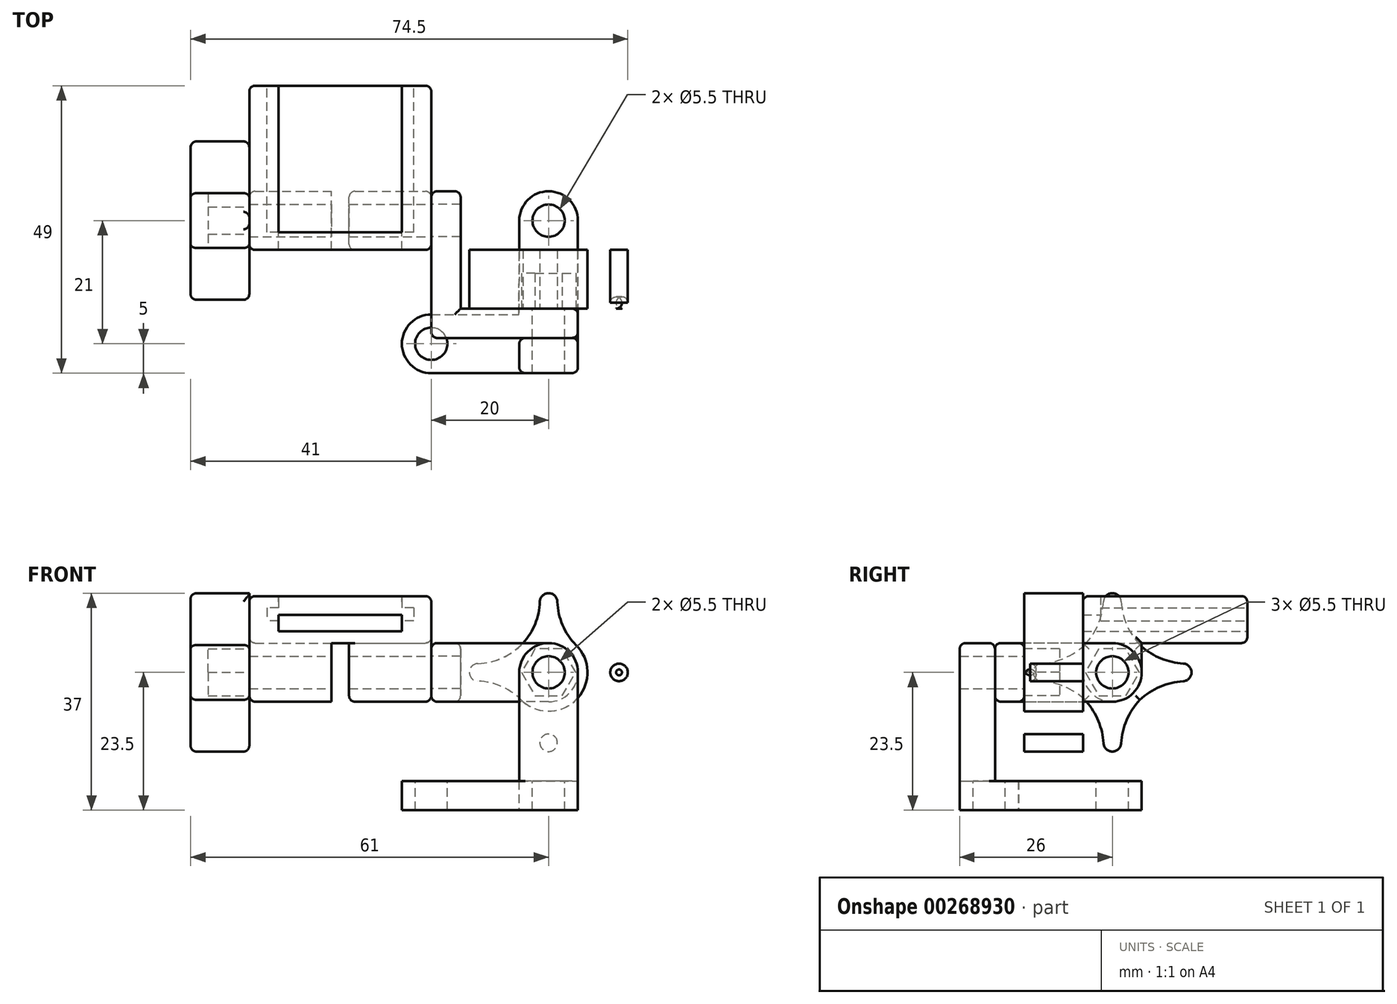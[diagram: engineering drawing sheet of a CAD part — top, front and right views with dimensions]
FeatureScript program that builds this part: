
annotation { "Feature Type Name" : "Feature", "Feature Type Description" : "" }
export const myFeature = defineFeature(function(context is Context, id is Id, definition is map)
    precondition{}
    {
        {
            var Q0;
            Q0=qCreatedBy(makeId("Top.planeOp"),FACE);
            var sketch = newSketch(context, id + "F0", { "sketchPlane" : qUnion([Q0])});
            skLineSegment(sketch, "E0.bottom", {"start": v(-15.5, 14) * mm, "end": v(15.5, 14) * mm});
            skLineSegment(sketch, "E0.top", {"start": v(-15.5, -14) * mm, "end": v(15.5, -14) * mm});
            skLineSegment(sketch, "E0.left", {"start": v(-15.5, 14) * mm, "end": v(-15.5, -14) * mm});
            skLineSegment(sketch, "E0.right", {"start": v(15.5, 14) * mm, "end": v(15.5, -14) * mm});
            skPoint(sketch, "E1", {"position": v(0, 14) * mm});
            skPoint(sketch, "E2", {"position": v(-15.5, 0) * mm});
            skSolve(sketch);
        }
        {
            var Q0;
            Q0=makeQuery(id+"F0.imprint","IMPRINT",FACE,{"disambiguationData":[TD([[makeQuery(id+"F0.imprint","IMPRINT",EDGE,{"derivedFrom":sQuery(id+"F0.wireOp",EDGE,"E0.bottom")}),-1.0]])]});
            extrude(context, id + "F1", {"entities" : qUnion([Q0]), "depth" : (4 + 4) * mm});
        }
        {
            var Q0;
            Q0=makeQuery(id+"F1.opExtrude","SWEPT_FACE",FACE,{"disambiguationData":[OSD([sQuery(id+"F0.wireOp",EDGE,"E0.bottom")])]});
            var sketch = newSketch(context, id + "F2", { "sketchPlane" : qUnion([Q0])});
            skLineSegment(sketch, "E3.bottom", {"start": v(-12.5, 6) * mm, "end": v(12.5, 6) * mm});
            skLineSegment(sketch, "E3.top", {"start": v(-12.5, 4.8) * mm, "end": v(12.5, 4.8) * mm});
            skLineSegment(sketch, "E3.left", {"start": v(-12.5, 6) * mm, "end": v(-12.5, 4.8) * mm});
            skLineSegment(sketch, "E3.right", {"start": v(12.5, 6) * mm, "end": v(12.5, 4.8) * mm});
            skLineSegment(sketch, "E4.bottom", {"start": v(-10.5, 8) * mm, "end": v(10.5, 8) * mm});
            skLineSegment(sketch, "E4.top", {"start": v(-10.5, 2) * mm, "end": v(10.5, 2) * mm});
            skLineSegment(sketch, "E4.left", {"start": v(-10.5, 8) * mm, "end": v(-10.5, 2) * mm});
            skLineSegment(sketch, "E4.right", {"start": v(10.5, 8) * mm, "end": v(10.5, 2) * mm});
            skSolve(sketch);
        }
        {
            var Q0;
            {var subQ5=sQuery(id+"F2.wireOp",EDGE,"E4.bottom");Q0=makeQuery(id+"F2.imprint","IMPRINT",FACE,{"disambiguationData":[TD([[makeQuery(id+"F2.imprint","IMPRINT",EDGE,{"derivedFrom":subQ5}),1.0]])]});}
            var Q1;
            {var subQ0=sQuery(id+"F2.wireOp",EDGE,"E4.left");var subQ1=sQuery(id+"F2.wireOp",EDGE,"E3.bottom");var subQ2=makeQuery(id+"F2.imprint","INTERSECT",VERTEX,{"derivedFrom":[subQ1,subQ0]});Q1=makeQuery(id+"F2.imprint","IMPRINT",FACE,{"disambiguationData":[TD([[makeQuery(id+"F2.imprint","IMPRINT",EDGE,{"disambiguationData":[TD([[subQ2,-1.0]])],"derivedFrom":subQ1}),-1.0]])]});}
            var Q2;
            {var subQ0=sQuery(id+"F2.wireOp",EDGE,"E3.left");Q2=makeQuery(id+"F2.imprint","IMPRINT",FACE,{"disambiguationData":[TD([[makeQuery(id+"F2.imprint","IMPRINT",EDGE,{"derivedFrom":subQ0}),1.0]])]});}
            var Q3;
            {var subQ5=sQuery(id+"F2.wireOp",EDGE,"E4.top");Q3=makeQuery(id+"F2.imprint","IMPRINT",FACE,{"disambiguationData":[TD([[makeQuery(id+"F2.imprint","IMPRINT",EDGE,{"derivedFrom":subQ5}),1.0]])]});}
            var Q4;
            {var subQ0=sQuery(id+"F2.wireOp",EDGE,"E3.right");Q4=makeQuery(id+"F2.imprint","IMPRINT",FACE,{"disambiguationData":[TD([[makeQuery(id+"F2.imprint","IMPRINT",EDGE,{"derivedFrom":subQ0}),-1.0]])]});}
            extrude(context, id + "F3", {"entities" : qUnion([Q0, Q1, Q2, Q3, Q4]), "operationType" : NewBodyOperationType.REMOVE, "oppositeDirection" : true, "depth" : 25 * mm});
        }
        {
            var Q0;
            Q0=makeQuery(id+"F3.boolean.opBoolean","COPY",FACE,{"derivedFrom":makeQuery(id+"F3.opExtrude","CAP_FACE",FACE,{"disambiguationData":[OSD([sQuery(id+"F2.wireOp",EDGE,"E3.bottom"),sQuery(id+"F2.wireOp",EDGE,"E3.top"),sQuery(id+"F2.wireOp",EDGE,"E3.left"),sQuery(id+"F2.wireOp",EDGE,"E3.right"),sQuery(id+"F2.wireOp",EDGE,"E4.bottom"),sQuery(id+"F2.wireOp",EDGE,"E4.top"),sQuery(id+"F2.wireOp",EDGE,"E4.left"),sQuery(id+"F2.wireOp",EDGE,"E4.right")])],"isStart":false})});
            var sketch = newSketch(context, id + "F4", { "sketchPlane" : qUnion([Q0])});
            skLineSegment(sketch, "E5.bottom", {"start": v(-10.5, 4.8) * mm, "end": v(10.5, 4.8) * mm});
            skLineSegment(sketch, "E5.top", {"start": v(-10.5, 2) * mm, "end": v(10.5, 2) * mm});
            skLineSegment(sketch, "E5.left", {"start": v(-10.5, 4.8) * mm, "end": v(-10.5, 2) * mm});
            skLineSegment(sketch, "E5.right", {"start": v(10.5, 4.8) * mm, "end": v(10.5, 2) * mm});
            skSolve(sketch);
        }
        {
            var Q0;
            Q0=makeQuery(id+"F4.imprint","IMPRINT",FACE,{"disambiguationData":[TD([[makeQuery(id+"F4.imprint","IMPRINT",EDGE,{"derivedFrom":sQuery(id+"F4.wireOp",EDGE,"E5.bottom")}),-1.0]])]});
            extrude(context, id + "F5", {"entities" : qUnion([Q0]), "operationType" : NewBodyOperationType.REMOVE, "endBound" : BoundingType.UP_TO_NEXT, "oppositeDirection" : true, "depth" : 25 * mm});
        }
        {
            var Q0;
            Q0=makeQuery(id+"F1.opExtrude","SWEPT_FACE",FACE,{"disambiguationData":[OSD([sQuery(id+"F0.wireOp",EDGE,"E0.right")])]});
            var sketch = newSketch(context, id + "F6", { "sketchPlane" : qUnion([Q0])});
            skLineSegment(sketch, "E6.bottom", {"start": v(-14, 0) * mm, "end": v(-4, 0) * mm});
            skLineSegment(sketch, "E6.top", {"start": v(-14, -10) * mm, "end": v(-4, -10) * mm});
            skLineSegment(sketch, "E6.left", {"start": v(-14, 0) * mm, "end": v(-14, -10) * mm});
            skLineSegment(sketch, "E6.right", {"start": v(-4, 0) * mm, "end": v(-4, -10) * mm});
            skCircle(sketch, "E7", {"center": v(-9, -5) * mm, "radius": 2.75 * mm});
            skPoint(sketch, "E8", {"position": v(-4, -5) * mm});
            skPoint(sketch, "E9", {"position": v(-9, -10) * mm});
            skCircle(sketch, "E10", {"center": v(-9, -5) * mm, "radius": 5 * mm});
            skSolve(sketch);
        }
        {
            var Q0;
            Q0=makeQuery(id+"F6.imprint","IMPRINT",FACE,{"disambiguationData":[TD([[makeQuery(id+"F6.imprint","IMPRINT",EDGE,{"derivedFrom":sQuery(id+"F6.wireOp",EDGE,"E7")}),-1.0]])]});
            var Q1;
            {var subQ0=sQuery(id+"F6.wireOp",EDGE,"E6.left");var subQ3=sQuery(id+"F6.wireOp",EDGE,"E10");var subQ5=makeQuery(id+"F6.imprint","INTERSECT",VERTEX,{"derivedFrom":[subQ0,subQ3]});Q1=makeQuery(id+"F6.imprint","IMPRINT",FACE,{"disambiguationData":[TD([[makeQuery(id+"F6.imprint","IMPRINT",EDGE,{"disambiguationData":[TD([[subQ5,1.0]])],"derivedFrom":subQ3}),-1.0]])]});}
            var Q2;
            {var subQ0=sQuery(id+"F6.wireOp",EDGE,"E6.right");var subQ3=sQuery(id+"F6.wireOp",EDGE,"E10");var subQ5=makeQuery(id+"F6.imprint","INTERSECT",VERTEX,{"derivedFrom":[subQ0,subQ3]});Q2=makeQuery(id+"F6.imprint","IMPRINT",FACE,{"disambiguationData":[TD([[makeQuery(id+"F6.imprint","IMPRINT",EDGE,{"disambiguationData":[TD([[subQ5,-1.0]])],"derivedFrom":subQ3}),-1.0]])]});}
            var Q3;
            Q3=makeQuery(id+"F1.opExtrude","SWEPT_FACE",FACE,{"disambiguationData":[OSD([sQuery(id+"F0.wireOp",EDGE,"E0.left")])]});
            extrude(context, id + "F7", {"entities" : qUnion([Q0, Q1, Q2]), "operationType" : NewBodyOperationType.ADD, "endBound" : BoundingType.UP_TO_SURFACE, "oppositeDirection" : true, "endBoundEntityFace" : qUnion([Q3]), "depth" : 25 * mm});
        }
        {
            var Q0;
            Q0=makeQuery(id+"F7.opExtrude","SWEPT_FACE",FACE,{"disambiguationData":[OSD([sQuery(id+"F6.wireOp",EDGE,"E6.right")])]});
            var sketch = newSketch(context, id + "F8", { "sketchPlane" : qUnion([Q0])});
            skLineSegment(sketch, "E11.bottom", {"start": v(-1.5, 0) * mm, "end": v(1.5, 0) * mm});
            skLineSegment(sketch, "E11.top", {"start": v(-1.5, -11.71) * mm, "end": v(1.5, -11.71) * mm});
            skLineSegment(sketch, "E11.left", {"start": v(-1.5, 0) * mm, "end": v(-1.5, -11.71) * mm});
            skLineSegment(sketch, "E11.right", {"start": v(1.5, 0) * mm, "end": v(1.5, -11.71) * mm});
            skPoint(sketch, "E12", {"position": v(0, 0) * mm});
            skSolve(sketch);
        }
        {
            var Q0;
            {var subQ0=sQuery(id+"F2.wireOp",EDGE,"E3.top");Q0=makeQuery(id+"F3.boolean.opBoolean","COPY",FACE,{"derivedFrom":makeQuery(id+"F3.opExtrude","SWEPT_FACE",FACE,{"disambiguationData":[OSD([subQ0]),TDD([makeQuery(id+"F2.imprint","IMPRINT",EDGE,{"disambiguationData":[TD([[makeQuery(id+"F2.imprint","INTERSECT",VERTEX,{"derivedFrom":[subQ0,sQuery(id+"F2.wireOp",EDGE,"E3.right")]}),1.0]])],"derivedFrom":subQ0})])]})});}
            var Q1;
            {var subQ0=sQuery(id+"F2.wireOp",EDGE,"E3.top");Q1=makeQuery(id+"F3.boolean.opBoolean","COPY",FACE,{"derivedFrom":makeQuery(id+"F3.opExtrude","SWEPT_FACE",FACE,{"disambiguationData":[OSD([subQ0]),TDD([makeQuery(id+"F2.imprint","IMPRINT",EDGE,{"disambiguationData":[TD([[makeQuery(id+"F2.imprint","INTERSECT",VERTEX,{"derivedFrom":[subQ0,sQuery(id+"F2.wireOp",EDGE,"E3.left")]}),-1.0]])],"derivedFrom":subQ0})])]})});}
            extrude(context, id + "F9", {"entities" : qUnion([Q0, Q1]), "operationType" : NewBodyOperationType.REMOVE, "oppositeDirection" : true, "depth" : 1 * mm});
        }
        {
            var Q0;
            {var subQ0=sQuery(id+"F8.wireOp",EDGE,"E11.bottom");Q0=makeQuery(id+"F8.imprint","IMPRINT",FACE,{"disambiguationData":[TD([[makeQuery(id+"F8.imprint","IMPRINT",EDGE,{"derivedFrom":subQ0}),1.0]])]});}
            var Q1;
            {var subQ0=sQuery(id+"F8.wireOp",EDGE,"E11.top");Q1=makeQuery(id+"F8.imprint","IMPRINT",FACE,{"disambiguationData":[TD([[makeQuery(id+"F8.imprint","IMPRINT",EDGE,{"derivedFrom":subQ0}),1.0]])]});}
            extrude(context, id + "F10", {"entities" : qUnion([Q0, Q1]), "operationType" : NewBodyOperationType.REMOVE, "endBound" : BoundingType.THROUGH_ALL, "oppositeDirection" : true, "depth" : 25 * mm});
        }
        {
            var Q0;
            Q0=makeQuery(id+"F1.opExtrude","CAP_EDGE",EDGE,{"disambiguationData":[OSD([sQuery(id+"F0.wireOp",EDGE,"E0.left")])],"isStart":false});
            var Q1;
            Q1=makeQuery(id+"F1.opExtrude","CAP_EDGE",EDGE,{"disambiguationData":[OSD([sQuery(id+"F0.wireOp",EDGE,"E0.left")])],"isStart":true});
            var Q2;
            Q2=makeQuery(id+"F1.opExtrude","CAP_EDGE",EDGE,{"disambiguationData":[OSD([sQuery(id+"F0.wireOp",EDGE,"E0.right")])],"isStart":true});
            var Q3;
            Q3=makeQuery(id+"F1.opExtrude","CAP_EDGE",EDGE,{"disambiguationData":[OSD([sQuery(id+"F0.wireOp",EDGE,"E0.right")])],"isStart":false});
            var Q4;
            Q4=makeQuery(id+"F3.boolean.opBoolean","COPY",EDGE,{"derivedFrom":makeQuery(id+"F3.opExtrude","SWEPT_EDGE",EDGE,{"disambiguationData":[OSD([sQuery(id+"F0.wireOp",EDGE,"E0.bottom"),sQuery(id+"F2.wireOp",EDGE,"E4.bottom"),sQuery(id+"F2.wireOp",EDGE,"E4.right")])]})});
            var Q5;
            Q5=makeQuery(id+"F3.boolean.opBoolean","COPY",EDGE,{"derivedFrom":makeQuery(id+"F3.opExtrude","SWEPT_EDGE",EDGE,{"disambiguationData":[OSD([sQuery(id+"F0.wireOp",EDGE,"E0.bottom"),sQuery(id+"F2.wireOp",EDGE,"E4.bottom"),sQuery(id+"F2.wireOp",EDGE,"E4.left")])]})});
            var Q6;
            Q6=makeQuery(id+"F3.boolean.opBoolean","COPY",EDGE,{"derivedFrom":makeQuery(id+"F3.opExtrude","CAP_EDGE",EDGE,{"disambiguationData":[OSD([sQuery(id+"F2.wireOp",EDGE,"E4.bottom")])],"isStart":false})});
            var Q7;
            Q7=makeQuery(id+"F5.boolean.opBoolean","COPY",EDGE,{"derivedFrom":makeQuery(id+"F5.opExtrude","CAP_EDGE",EDGE,{"disambiguationData":[OSD([sQuery(id+"F4.wireOp",EDGE,"E5.bottom")])],"isStart":true})});
            var Q8;
            Q8=makeQuery(id+"F1.opExtrude","CAP_EDGE",EDGE,{"disambiguationData":[OSD([sQuery(id+"F0.wireOp",EDGE,"E0.bottom")])],"isStart":true});
            var Q9;
            Q9=makeQuery(id+"F1.opExtrude","SWEPT_EDGE",EDGE,{"disambiguationData":[OSD([sQuery(id+"F0.wireOp",EDGE,"E0.bottom"),sQuery(id+"F0.wireOp",EDGE,"E0.left")])]});
            var Q10;
            Q10=makeQuery(id+"F1.opExtrude","SWEPT_EDGE",EDGE,{"disambiguationData":[OSD([sQuery(id+"F0.wireOp",EDGE,"E0.bottom"),sQuery(id+"F0.wireOp",EDGE,"E0.right")])]});
            var Q11;
            {var subQ0=sQuery(id+"F0.wireOp",EDGE,"E0.bottom");var subQ2=makeQuery(id+"F1.opExtrude","CAP_EDGE",EDGE,{"disambiguationData":[OSD([subQ0])],"isStart":false});var subQ3=sQuery(id+"F0.wireOp",EDGE,"E0.right");Q11=makeQuery(id+"F3.boolean.opBoolean","SPLIT",EDGE,{"disambiguationData":[TD([makeQuery(id+"F1.opExtrude","SWEPT_FACE",FACE,{"disambiguationData":[OSD([subQ3])]})])],"derivedFrom":subQ2});}
            var Q12;
            {var subQ0=sQuery(id+"F0.wireOp",EDGE,"E0.bottom");var subQ1=sQuery(id+"F0.wireOp",EDGE,"E0.left");var subQ3=makeQuery(id+"F1.opExtrude","CAP_EDGE",EDGE,{"disambiguationData":[OSD([subQ0])],"isStart":false});Q12=makeQuery(id+"F3.boolean.opBoolean","SPLIT",EDGE,{"disambiguationData":[TD([makeQuery(id+"F1.opExtrude","SWEPT_FACE",FACE,{"disambiguationData":[OSD([subQ1])]})])],"derivedFrom":subQ3});}
            var Q13;
            Q13=makeQuery(id+"F3.boolean.opBoolean","COPY",EDGE,{"derivedFrom":makeQuery(id+"F3.opExtrude","CAP_EDGE",EDGE,{"disambiguationData":[OSD([sQuery(id+"F2.wireOp",EDGE,"E4.top")])],"isStart":true})});
            var Q14;
            {var subQ0=sQuery(id+"F2.wireOp",EDGE,"E4.left");Q14=makeQuery(id+"F3.boolean.opBoolean","COPY",EDGE,{"derivedFrom":makeQuery(id+"F3.opExtrude","CAP_EDGE",EDGE,{"disambiguationData":[OSD([subQ0]),TDD([makeQuery(id+"F2.imprint","IMPRINT",EDGE,{"disambiguationData":[TD([[makeQuery(id+"F2.imprint","INTERSECT",VERTEX,{"derivedFrom":[sQuery(id+"F2.wireOp",EDGE,"E4.top"),subQ0]}),1.0]])],"derivedFrom":subQ0})])],"isStart":true})});}
            var Q15;
            {var subQ0=sQuery(id+"F2.wireOp",EDGE,"E4.right");Q15=makeQuery(id+"F3.boolean.opBoolean","COPY",EDGE,{"derivedFrom":makeQuery(id+"F3.opExtrude","CAP_EDGE",EDGE,{"disambiguationData":[OSD([subQ0]),TDD([makeQuery(id+"F2.imprint","IMPRINT",EDGE,{"disambiguationData":[TD([[makeQuery(id+"F2.imprint","INTERSECT",VERTEX,{"derivedFrom":[sQuery(id+"F2.wireOp",EDGE,"E4.top"),subQ0]}),1.0]])],"derivedFrom":subQ0})])],"isStart":true})});}
            var Q16;
            Q16=makeQuery(id+"F3.boolean.opBoolean","COPY",EDGE,{"derivedFrom":makeQuery(id+"F3.opExtrude","CAP_EDGE",EDGE,{"disambiguationData":[OSD([sQuery(id+"F2.wireOp",EDGE,"E3.left")])],"isStart":true})});
            var Q17;
            {var subQ0=sQuery(id+"F2.wireOp",EDGE,"E3.top");Q17=makeQuery(id+"F3.boolean.opBoolean","COPY",EDGE,{"derivedFrom":makeQuery(id+"F3.opExtrude","CAP_EDGE",EDGE,{"disambiguationData":[OSD([subQ0]),TDD([makeQuery(id+"F2.imprint","IMPRINT",EDGE,{"disambiguationData":[TD([[makeQuery(id+"F2.imprint","INTERSECT",VERTEX,{"derivedFrom":[subQ0,sQuery(id+"F2.wireOp",EDGE,"E3.left")]}),-1.0]])],"derivedFrom":subQ0})])],"isStart":true})});}
            var Q18;
            {var subQ0=sQuery(id+"F2.wireOp",EDGE,"E3.bottom");Q18=makeQuery(id+"F3.boolean.opBoolean","COPY",EDGE,{"derivedFrom":makeQuery(id+"F3.opExtrude","CAP_EDGE",EDGE,{"disambiguationData":[OSD([subQ0]),TDD([makeQuery(id+"F2.imprint","IMPRINT",EDGE,{"disambiguationData":[TD([[makeQuery(id+"F2.imprint","INTERSECT",VERTEX,{"derivedFrom":[subQ0,sQuery(id+"F2.wireOp",EDGE,"E3.left")]}),-1.0]])],"derivedFrom":subQ0})])],"isStart":true})});}
            var Q19;
            Q19=makeQuery(id+"F3.boolean.opBoolean","COPY",EDGE,{"derivedFrom":makeQuery(id+"F3.opExtrude","CAP_EDGE",EDGE,{"disambiguationData":[OSD([sQuery(id+"F2.wireOp",EDGE,"E3.right")])],"isStart":true})});
            var Q20;
            {var subQ0=sQuery(id+"F2.wireOp",EDGE,"E3.top");Q20=makeQuery(id+"F3.boolean.opBoolean","COPY",EDGE,{"derivedFrom":makeQuery(id+"F3.opExtrude","CAP_EDGE",EDGE,{"disambiguationData":[OSD([subQ0]),TDD([makeQuery(id+"F2.imprint","IMPRINT",EDGE,{"disambiguationData":[TD([[makeQuery(id+"F2.imprint","INTERSECT",VERTEX,{"derivedFrom":[subQ0,sQuery(id+"F2.wireOp",EDGE,"E3.right")]}),1.0]])],"derivedFrom":subQ0})])],"isStart":true})});}
            var Q21;
            {var subQ0=sQuery(id+"F2.wireOp",EDGE,"E3.bottom");Q21=makeQuery(id+"F3.boolean.opBoolean","COPY",EDGE,{"derivedFrom":makeQuery(id+"F3.opExtrude","CAP_EDGE",EDGE,{"disambiguationData":[OSD([subQ0]),TDD([makeQuery(id+"F2.imprint","IMPRINT",EDGE,{"disambiguationData":[TD([[makeQuery(id+"F2.imprint","INTERSECT",VERTEX,{"derivedFrom":[subQ0,sQuery(id+"F2.wireOp",EDGE,"E3.right")]}),1.0]])],"derivedFrom":subQ0})])],"isStart":true})});}
            var Q22;
            {var subQ0=sQuery(id+"F2.wireOp",EDGE,"E4.right");Q22=makeQuery(id+"F3.boolean.opBoolean","COPY",EDGE,{"derivedFrom":makeQuery(id+"F3.opExtrude","CAP_EDGE",EDGE,{"disambiguationData":[OSD([subQ0]),TDD([makeQuery(id+"F2.imprint","IMPRINT",EDGE,{"disambiguationData":[TD([[makeQuery(id+"F2.imprint","INTERSECT",VERTEX,{"derivedFrom":[sQuery(id+"F2.wireOp",EDGE,"E3.bottom"),subQ0]}),1.0]])],"derivedFrom":subQ0})])],"isStart":true})});}
            var Q23;
            {var subQ0=sQuery(id+"F2.wireOp",EDGE,"E4.left");Q23=makeQuery(id+"F3.boolean.opBoolean","COPY",EDGE,{"derivedFrom":makeQuery(id+"F3.opExtrude","CAP_EDGE",EDGE,{"disambiguationData":[OSD([subQ0]),TDD([makeQuery(id+"F2.imprint","IMPRINT",EDGE,{"disambiguationData":[TD([[makeQuery(id+"F2.imprint","INTERSECT",VERTEX,{"derivedFrom":[sQuery(id+"F2.wireOp",EDGE,"E3.bottom"),subQ0]}),1.0]])],"derivedFrom":subQ0})])],"isStart":true})});}
            var Q24;
            Q24=makeQuery(id+"F5.boolean.opBoolean","COPY",EDGE,{"derivedFrom":makeQuery(id+"F5.opExtrude","TWEAK_EDGE",EDGE,{"derivedFrom":[makeQuery(id+"F1.opExtrude","SWEPT_FACE",FACE,{"disambiguationData":[OSD([sQuery(id+"F0.wireOp",EDGE,"E0.top")])]}),makeQuery(id+"F4.imprint","IMPRINT",EDGE,{"derivedFrom":sQuery(id+"F4.wireOp",EDGE,"E5.top")})]})});
            var Q25;
            Q25=makeQuery(id+"F5.boolean.opBoolean","COPY",EDGE,{"derivedFrom":makeQuery(id+"F5.opExtrude","TWEAK_EDGE",EDGE,{"derivedFrom":[makeQuery(id+"F1.opExtrude","SWEPT_FACE",FACE,{"disambiguationData":[OSD([sQuery(id+"F0.wireOp",EDGE,"E0.top")])]}),makeQuery(id+"F4.imprint","IMPRINT",EDGE,{"derivedFrom":sQuery(id+"F4.wireOp",EDGE,"E5.bottom")})]})});
            var Q26;
            Q26=makeQuery(id+"F5.boolean.opBoolean","COPY",EDGE,{"derivedFrom":makeQuery(id+"F5.opExtrude","TWEAK_EDGE",EDGE,{"derivedFrom":[makeQuery(id+"F1.opExtrude","SWEPT_FACE",FACE,{"disambiguationData":[OSD([sQuery(id+"F0.wireOp",EDGE,"E0.top")])]}),makeQuery(id+"F4.imprint","IMPRINT",EDGE,{"derivedFrom":sQuery(id+"F4.wireOp",EDGE,"E5.left")})]})});
            var Q27;
            Q27=makeQuery(id+"F5.boolean.opBoolean","COPY",EDGE,{"derivedFrom":makeQuery(id+"F5.opExtrude","TWEAK_EDGE",EDGE,{"derivedFrom":[makeQuery(id+"F1.opExtrude","SWEPT_FACE",FACE,{"disambiguationData":[OSD([sQuery(id+"F0.wireOp",EDGE,"E0.top")])]}),makeQuery(id+"F4.imprint","IMPRINT",EDGE,{"derivedFrom":sQuery(id+"F4.wireOp",EDGE,"E5.right")})]})});
            var Q28;
            Q28=makeQuery(id+"F1.opExtrude","CAP_EDGE",EDGE,{"disambiguationData":[OSD([sQuery(id+"F0.wireOp",EDGE,"E0.top")])],"isStart":false});
            var Q29;
            Q29=makeQuery(id+"F1.opExtrude","SWEPT_EDGE",EDGE,{"disambiguationData":[OSD([sQuery(id+"F0.wireOp",EDGE,"E0.top"),sQuery(id+"F0.wireOp",EDGE,"E0.right")])]});
            var Q30;
            Q30=makeQuery(id+"F1.opExtrude","CAP_EDGE",EDGE,{"disambiguationData":[OSD([sQuery(id+"F0.wireOp",EDGE,"E0.top")])],"isStart":true});
            var Q31;
            Q31=makeQuery(id+"F1.opExtrude","SWEPT_EDGE",EDGE,{"disambiguationData":[OSD([sQuery(id+"F0.wireOp",EDGE,"E0.top"),sQuery(id+"F0.wireOp",EDGE,"E0.left")])]});
            var Q32;
            Q32=makeQuery(id+"F10.boolean.opBoolean","COPY",EDGE,{"derivedFrom":makeQuery(id+"F10.opExtrude","CAP_EDGE",EDGE,{"disambiguationData":[OSD([sQuery(id+"F8.wireOp",EDGE,"E11.left")])],"isStart":true})});
            var Q33;
            Q33=makeQuery(id+"F10.boolean.opBoolean","COPY",EDGE,{"derivedFrom":makeQuery(id+"F10.opExtrude","CAP_EDGE",EDGE,{"disambiguationData":[OSD([sQuery(id+"F8.wireOp",EDGE,"E11.right")])],"isStart":true})});
            var Q34;
            {var subQ0=sQuery(id+"F2.wireOp",EDGE,"E3.top");Q34=makeQuery(id+"F9.boolean.opBoolean","COPY",EDGE,{"derivedFrom":makeQuery(id+"F9.opExtrude","CAP_EDGE",EDGE,{"disambiguationData":[OSD([subQ0]),TDD([makeQuery(id+"F3.boolean.opBoolean","COPY",EDGE,{"derivedFrom":makeQuery(id+"F3.opExtrude","CAP_EDGE",EDGE,{"disambiguationData":[OSD([subQ0]),TDD([makeQuery(id+"F2.imprint","IMPRINT",EDGE,{"disambiguationData":[TD([[makeQuery(id+"F2.imprint","INTERSECT",VERTEX,{"derivedFrom":[subQ0,sQuery(id+"F2.wireOp",EDGE,"E3.right")]}),1.0]])],"derivedFrom":subQ0})])],"isStart":true})})])],"isStart":false})});}
            var Q35;
            {var subQ0=sQuery(id+"F2.wireOp",EDGE,"E3.top");Q35=makeQuery(id+"F9.boolean.opBoolean","COPY",EDGE,{"derivedFrom":makeQuery(id+"F9.opExtrude","CAP_EDGE",EDGE,{"disambiguationData":[OSD([subQ0]),TDD([makeQuery(id+"F3.boolean.opBoolean","COPY",EDGE,{"derivedFrom":makeQuery(id+"F3.opExtrude","CAP_EDGE",EDGE,{"disambiguationData":[OSD([subQ0]),TDD([makeQuery(id+"F2.imprint","IMPRINT",EDGE,{"disambiguationData":[TD([[makeQuery(id+"F2.imprint","INTERSECT",VERTEX,{"derivedFrom":[subQ0,sQuery(id+"F2.wireOp",EDGE,"E3.left")]}),-1.0]])],"derivedFrom":subQ0})])],"isStart":true})})])],"isStart":false})});}
            fillet(context, id + "F11", {"entities" : qUnion([Q0, Q1, Q2, Q3, Q4, Q5, Q6, Q7, Q8, Q9, Q10, Q11, Q12, Q13, Q14, Q15, Q16, Q17, Q18, Q19, Q20, Q21, Q22, Q23, Q24, Q25, Q26, Q27, Q28, Q29, Q30, Q31, Q32, Q33, Q34, Q35]), "radius" : 1 * mm, "tangentPropagation" : true, "allowEdgeOverflow" : false});
        }
        {
            var Q0;
            {var subQ0=sQuery(id+"F0.wireOp",EDGE,"E0.left");Q0=makeQuery(id+"F7.boolean.opBoolean","MERGE",FACE,{"derivedFrom":[makeQuery(id+"F1.opExtrude","SWEPT_FACE",FACE,{"disambiguationData":[OSD([subQ0])]}),makeQuery(id+"F7.opExtrude","CAP_FACE",FACE,{"disambiguationData":[OSD([subQ0])],"isStart":false})]});}
            var sketch = newSketch(context, id + "F12", { "sketchPlane" : qUnion([Q0])});
            skCircle(sketch, "E13.cCircle", {"center": v(9, -5) * mm, "radius": 4 * mm, "construction": true});
            skLineSegment(sketch, "E13.0", {"start": v(6.7, -1) * mm, "end": v(11.3, -1) * mm});
            skLineSegment(sketch, "E13.1", {"start": v(11.3, -1) * mm, "end": v(13.62, -5) * mm});
            skLineSegment(sketch, "E13.2", {"start": v(13.62, -5) * mm, "end": v(11.3, -9) * mm});
            skLineSegment(sketch, "E13.3", {"start": v(11.3, -9) * mm, "end": v(6.7, -9) * mm});
            skLineSegment(sketch, "E13.4", {"start": v(6.7, -9) * mm, "end": v(4.38, -5) * mm});
            skLineSegment(sketch, "E13.5", {"start": v(4.38, -5) * mm, "end": v(6.7, -1) * mm});
            skPoint(sketch, "E13.0.midPoint", {"position": v(9, -1) * mm});
            skCircle(sketch, "E14", {"center": v(9, -5) * mm, "radius": 6.62 * mm});
            skCircle(sketch, "E15", {"center": v(9, 7) * mm, "radius": 1.5 * mm});
            skLineSegment(sketch, "E16", {"start": v(9, -5) * mm, "end": v(4.32, -0.32) * mm});
            skLineSegment(sketch, "E17", {"start": v(9, -5) * mm, "end": v(13.68, -0.32) * mm});
            skArc(sketch, "E18", {"start": v(4.32, -0.32) * mm, "mid": v(6.55, 3.11) * mm, "end": v(7.5, 7.1) * mm});
            skArc(sketch, "E19", {"start": v(10.5, 7.1) * mm, "mid": v(11.45, 3.11) * mm, "end": v(13.68, -0.32) * mm});
            skArc(sketch, "E20.1.0", {"start": v(-3.1, -3.5) * mm, "mid": v(0.89, -2.55) * mm, "end": v(4.32, -0.32) * mm});
            skArc(sketch, "E20.1.1", {"start": v(4.32, -9.68) * mm, "mid": v(0.89, -7.45) * mm, "end": v(-3.1, -6.5) * mm});
            skCircle(sketch, "E20.1.2", {"center": v(-3, -5) * mm, "radius": 1.5 * mm});
            skArc(sketch, "E20.2.0", {"start": v(7.5, -17.1) * mm, "mid": v(6.55, -13.11) * mm, "end": v(4.32, -9.68) * mm});
            skArc(sketch, "E20.2.1", {"start": v(13.68, -9.68) * mm, "mid": v(11.45, -13.11) * mm, "end": v(10.5, -17.1) * mm});
            skCircle(sketch, "E20.2.2", {"center": v(9, -17) * mm, "radius": 1.5 * mm});
            skArc(sketch, "E20.3.0", {"start": v(21.1, -6.5) * mm, "mid": v(17.11, -7.45) * mm, "end": v(13.68, -9.68) * mm});
            skArc(sketch, "E20.3.1", {"start": v(13.68, -0.32) * mm, "mid": v(17.11, -2.55) * mm, "end": v(21.1, -3.5) * mm});
            skCircle(sketch, "E20.3.2", {"center": v(21, -5) * mm, "radius": 1.5 * mm});
            skSolve(sketch);
        }
        {
            var Q0;
            {var subQ1=sQuery(id+"F0.wireOp",EDGE,"E0.left");var subQ2=makeQuery(id+"F1.opExtrude","SWEPT_FACE",FACE,{"disambiguationData":[OSD([subQ1])]});var subQ3=makeQuery(id+"F7.boolean.opBoolean","MERGE",FACE,{"derivedFrom":[subQ2,makeQuery(id+"F7.opExtrude","CAP_FACE",FACE,{"disambiguationData":[OSD([subQ1])],"isStart":false})]});var subQ4=makeQuery(id+"F11.opFillet","BLEND_EDGE",EDGE,{"blendedFrom":[makeQuery(id+"F1.opExtrude","CAP_EDGE",EDGE,{"disambiguationData":[OSD([subQ1])],"isStart":false}),subQ3],"blendedInto":[subQ3]});var subQ18=sQuery(id+"F12.wireOp",EDGE,"E15");var subQ19=makeQuery(id+"F12.imprint","INTERSECT",VERTEX,{"disambiguationData":[OD(0.0)],"derivedFrom":[subQ4,subQ18]});Q0=makeQuery(id+"F12.imprint","IMPRINT",FACE,{"disambiguationData":[TD([[makeQuery(id+"F12.imprint","IMPRINT",EDGE,{"disambiguationData":[TD([[subQ19,-1.0]])],"derivedFrom":subQ18}),-1.0]])]});}
            var Q1;
            {var subQ0=sQuery(id+"F12.wireOp",EDGE,"E15");var subQ1=sQuery(id+"F0.wireOp",EDGE,"E0.left");var subQ2=makeQuery(id+"F11.opFillet","BLEND_EDGE",EDGE,{"blendedFrom":[makeQuery(id+"F1.opExtrude","CAP_EDGE",EDGE,{"disambiguationData":[OSD([subQ1])],"isStart":false}),makeQuery(id+"F7.boolean.opBoolean","MERGE",FACE,{"derivedFrom":[makeQuery(id+"F1.opExtrude","SWEPT_FACE",FACE,{"disambiguationData":[OSD([subQ1])]}),makeQuery(id+"F7.opExtrude","CAP_FACE",FACE,{"disambiguationData":[OSD([subQ1])],"isStart":false})]})],"blendedInto":[makeQuery(id+"F7.boolean.opBoolean","MERGE",FACE,{"derivedFrom":[makeQuery(id+"F1.opExtrude","SWEPT_FACE",FACE,{"disambiguationData":[OSD([subQ1])]}),makeQuery(id+"F7.opExtrude","CAP_FACE",FACE,{"disambiguationData":[OSD([subQ1])],"isStart":false})]})]});var subQ3=makeQuery(id+"F12.imprint","INTERSECT",VERTEX,{"disambiguationData":[OD(0.0)],"derivedFrom":[subQ2,subQ0]});Q1=makeQuery(id+"F12.imprint","IMPRINT",FACE,{"disambiguationData":[TD([[makeQuery(id+"F12.imprint","IMPRINT",EDGE,{"disambiguationData":[TD([[subQ3,-1.0]])],"derivedFrom":subQ0}),1.0]])]});}
            var Q2;
            {var subQ0=sQuery(id+"F12.wireOp",EDGE,"E15");var subQ1=makeQuery(id+"F12.imprint","INTERSECT",VERTEX,{"derivedFrom":[subQ0,sQuery(id+"F12.wireOp",EDGE,"E18")]});Q2=makeQuery(id+"F12.imprint","IMPRINT",FACE,{"disambiguationData":[TD([[makeQuery(id+"F12.imprint","IMPRINT",EDGE,{"disambiguationData":[TD([[subQ1,1.0]])],"derivedFrom":subQ0}),1.0]])]});}
            var Q3;
            {var subQ0=sQuery(id+"F12.wireOp",EDGE,"E20.1.2");var subQ1=makeQuery(id+"F12.imprint","INTERSECT",VERTEX,{"derivedFrom":[sQuery(id+"F12.wireOp",EDGE,"E20.1.0"),subQ0]});Q3=makeQuery(id+"F12.imprint","IMPRINT",FACE,{"disambiguationData":[TD([[makeQuery(id+"F12.imprint","IMPRINT",EDGE,{"disambiguationData":[TD([[subQ1,-1.0]])],"derivedFrom":subQ0}),1.0]])]});}
            var Q4;
            {var subQ0=sQuery(id+"F12.wireOp",EDGE,"E20.1.0");Q4=makeQuery(id+"F12.imprint","IMPRINT",FACE,{"disambiguationData":[TD([[makeQuery(id+"F12.imprint","IMPRINT",EDGE,{"derivedFrom":subQ0}),-1.0]])]});}
            var Q5;
            {var subQ0=sQuery(id+"F12.wireOp",EDGE,"E20.2.0");Q5=makeQuery(id+"F12.imprint","IMPRINT",FACE,{"disambiguationData":[TD([[makeQuery(id+"F12.imprint","IMPRINT",EDGE,{"derivedFrom":subQ0}),-1.0]])]});}
            var Q6;
            {var subQ0=sQuery(id+"F12.wireOp",EDGE,"E20.2.2");var subQ1=makeQuery(id+"F12.imprint","INTERSECT",VERTEX,{"derivedFrom":[sQuery(id+"F12.wireOp",EDGE,"E20.2.0"),subQ0]});Q6=makeQuery(id+"F12.imprint","IMPRINT",FACE,{"disambiguationData":[TD([[makeQuery(id+"F12.imprint","IMPRINT",EDGE,{"disambiguationData":[TD([[subQ1,-1.0]])],"derivedFrom":subQ0}),1.0]])]});}
            var Q7;
            {var subQ2=sQuery(id+"F12.wireOp",EDGE,"E20.3.0");Q7=makeQuery(id+"F12.imprint","IMPRINT",FACE,{"disambiguationData":[TD([[makeQuery(id+"F12.imprint","IMPRINT",EDGE,{"derivedFrom":subQ2}),-1.0]])]});}
            var Q8;
            {var subQ0=sQuery(id+"F12.wireOp",EDGE,"E20.3.2");var subQ1=makeQuery(id+"F12.imprint","INTERSECT",VERTEX,{"derivedFrom":[sQuery(id+"F12.wireOp",EDGE,"E20.3.0"),subQ0]});Q8=makeQuery(id+"F12.imprint","IMPRINT",FACE,{"disambiguationData":[TD([[makeQuery(id+"F12.imprint","IMPRINT",EDGE,{"disambiguationData":[TD([[subQ1,-1.0]])],"derivedFrom":subQ0}),1.0]])]});}
            var Q9;
            {var subQ0=sQuery(id+"F12.wireOp",EDGE,"E14");var subQ1=makeQuery(id+"F12.imprint","INTERSECT",VERTEX,{"derivedFrom":[subQ0,sQuery(id+"F12.wireOp",EDGE,"E20.1.1"),sQuery(id+"F12.wireOp",EDGE,"E20.2.0")]});Q9=makeQuery(id+"F12.imprint","IMPRINT",FACE,{"disambiguationData":[TD([[makeQuery(id+"F12.imprint","IMPRINT",EDGE,{"disambiguationData":[TD([[subQ1,-1.0]])],"derivedFrom":subQ0}),1.0]])]});}
            var Q10;
            {var subQ19=sQuery(id+"F12.wireOp",EDGE,"E13.0");Q10=makeQuery(id+"F12.imprint","IMPRINT",FACE,{"disambiguationData":[TD([[makeQuery(id+"F12.imprint","IMPRINT",EDGE,{"derivedFrom":subQ19}),1.0]])]});}
            var Q11;
            {var subQ0=sQuery(id+"F12.wireOp",EDGE,"E18");var subQ1=sQuery(id+"F12.wireOp",EDGE,"E14");var subQ2=makeQuery(id+"F12.imprint","INTERSECT",VERTEX,{"derivedFrom":[subQ1,sQuery(id+"F12.wireOp",EDGE,"E16"),subQ0,sQuery(id+"F12.wireOp",EDGE,"E20.1.0")]});Q11=makeQuery(id+"F12.imprint","IMPRINT",FACE,{"disambiguationData":[TD([[makeQuery(id+"F12.imprint","IMPRINT",EDGE,{"disambiguationData":[TD([[subQ2,1.0]])],"derivedFrom":subQ1}),-1.0]])]});}
            var Q12;
            {var subQ0=sQuery(id+"F12.wireOp",EDGE,"E16");var subQ1=sQuery(id+"F12.wireOp",EDGE,"E13.5");var subQ2=makeQuery(id+"F12.imprint","INTERSECT",VERTEX,{"derivedFrom":[subQ1,subQ0]});Q12=makeQuery(id+"F12.imprint","IMPRINT",FACE,{"disambiguationData":[TD([[makeQuery(id+"F12.imprint","IMPRINT",EDGE,{"disambiguationData":[TD([[subQ2,1.0]])],"derivedFrom":subQ1}),1.0]])]});}
            var Q13;
            {var subQ0=sQuery(id+"F12.wireOp",EDGE,"E16");var subQ1=sQuery(id+"F12.wireOp",EDGE,"E14");var subQ2=makeQuery(id+"F12.imprint","INTERSECT",VERTEX,{"derivedFrom":[subQ1,subQ0,sQuery(id+"F12.wireOp",EDGE,"E18"),sQuery(id+"F12.wireOp",EDGE,"E20.1.0")]});Q13=makeQuery(id+"F12.imprint","IMPRINT",FACE,{"disambiguationData":[TD([[makeQuery(id+"F12.imprint","IMPRINT",EDGE,{"disambiguationData":[TD([[subQ2,1.0]])],"derivedFrom":subQ1}),1.0]])]});}
            var Q14;
            {var subQ0=sQuery(id+"F12.wireOp",EDGE,"E17");var subQ1=sQuery(id+"F12.wireOp",EDGE,"E13.1");var subQ2=makeQuery(id+"F12.imprint","INTERSECT",VERTEX,{"derivedFrom":[subQ1,subQ0]});Q14=makeQuery(id+"F12.imprint","IMPRINT",FACE,{"disambiguationData":[TD([[makeQuery(id+"F12.imprint","IMPRINT",EDGE,{"disambiguationData":[TD([[subQ2,-1.0]])],"derivedFrom":subQ1}),1.0]])]});}
            var Q15;
            {var subQ0=sQuery(id+"F12.wireOp",EDGE,"E17");var subQ1=sQuery(id+"F12.wireOp",EDGE,"E14");var subQ2=makeQuery(id+"F12.imprint","INTERSECT",VERTEX,{"derivedFrom":[subQ1,subQ0,sQuery(id+"F12.wireOp",EDGE,"E19"),sQuery(id+"F12.wireOp",EDGE,"E20.3.1")]});Q15=makeQuery(id+"F12.imprint","IMPRINT",FACE,{"disambiguationData":[TD([[makeQuery(id+"F12.imprint","IMPRINT",EDGE,{"disambiguationData":[TD([[subQ2,-1.0]])],"derivedFrom":subQ1}),1.0]])]});}
            var Q16;
            {var subQ0=sQuery(id+"F12.wireOp",EDGE,"E19");var subQ1=sQuery(id+"F12.wireOp",EDGE,"E14");var subQ2=makeQuery(id+"F12.imprint","INTERSECT",VERTEX,{"derivedFrom":[subQ1,sQuery(id+"F12.wireOp",EDGE,"E17"),subQ0,sQuery(id+"F12.wireOp",EDGE,"E20.3.1")]});Q16=makeQuery(id+"F12.imprint","IMPRINT",FACE,{"disambiguationData":[TD([[makeQuery(id+"F12.imprint","IMPRINT",EDGE,{"disambiguationData":[TD([[subQ2,-1.0]])],"derivedFrom":subQ1}),-1.0]])]});}
            var Q17;
            {var subQ0=sQuery(id+"F12.wireOp",EDGE,"E18");var subQ1=sQuery(id+"F12.wireOp",EDGE,"E15");var subQ2=makeQuery(id+"F12.imprint","INTERSECT",VERTEX,{"derivedFrom":[subQ1,subQ0]});Q17=makeQuery(id+"F12.imprint","IMPRINT",FACE,{"disambiguationData":[TD([[makeQuery(id+"F12.imprint","IMPRINT",EDGE,{"disambiguationData":[TD([[subQ2,-1.0]])],"derivedFrom":subQ1}),-1.0]])]});}
            var Q18;
            {var subQ0=sQuery(id+"F12.wireOp",EDGE,"E19");var subQ1=sQuery(id+"F12.wireOp",EDGE,"E15");var subQ2=makeQuery(id+"F12.imprint","INTERSECT",VERTEX,{"derivedFrom":[subQ1,subQ0]});Q18=makeQuery(id+"F12.imprint","IMPRINT",FACE,{"disambiguationData":[TD([[makeQuery(id+"F12.imprint","IMPRINT",EDGE,{"disambiguationData":[TD([[subQ2,1.0]])],"derivedFrom":subQ1}),-1.0]])]});}
            var Q19;
            {var subQ1=sQuery(id+"F0.wireOp",EDGE,"E0.left");var subQ2=makeQuery(id+"F1.opExtrude","SWEPT_FACE",FACE,{"disambiguationData":[OSD([subQ1])]});var subQ3=makeQuery(id+"F7.boolean.opBoolean","MERGE",FACE,{"derivedFrom":[subQ2,makeQuery(id+"F7.opExtrude","CAP_FACE",FACE,{"disambiguationData":[OSD([subQ1])],"isStart":false})]});var subQ4=makeQuery(id+"F11.opFillet","BLEND_EDGE",EDGE,{"blendedFrom":[makeQuery(id+"F1.opExtrude","CAP_EDGE",EDGE,{"disambiguationData":[OSD([subQ1])],"isStart":false}),subQ3],"blendedInto":[subQ3]});var subQ18=sQuery(id+"F12.wireOp",EDGE,"E15");var subQ20=makeQuery(id+"F12.imprint","INTERSECT",VERTEX,{"disambiguationData":[OD(0.0)],"derivedFrom":[subQ4,subQ18]});Q19=makeQuery(id+"F12.imprint","IMPRINT",FACE,{"disambiguationData":[TD([[makeQuery(id+"F12.imprint","IMPRINT",EDGE,{"disambiguationData":[TD([[subQ20,1.0]])],"derivedFrom":subQ18}),-1.0]])]});}
            var Q20;
            {var subQ0=sQuery(id+"F12.wireOp",EDGE,"E15");var subQ1=sQuery(id+"F0.wireOp",EDGE,"E0.left");var subQ2=makeQuery(id+"F11.opFillet","BLEND_EDGE",EDGE,{"blendedFrom":[makeQuery(id+"F1.opExtrude","CAP_EDGE",EDGE,{"disambiguationData":[OSD([subQ1])],"isStart":false}),makeQuery(id+"F7.boolean.opBoolean","MERGE",FACE,{"derivedFrom":[makeQuery(id+"F1.opExtrude","SWEPT_FACE",FACE,{"disambiguationData":[OSD([subQ1])]}),makeQuery(id+"F7.opExtrude","CAP_FACE",FACE,{"disambiguationData":[OSD([subQ1])],"isStart":false})]})],"blendedInto":[makeQuery(id+"F7.boolean.opBoolean","MERGE",FACE,{"derivedFrom":[makeQuery(id+"F1.opExtrude","SWEPT_FACE",FACE,{"disambiguationData":[OSD([subQ1])]}),makeQuery(id+"F7.opExtrude","CAP_FACE",FACE,{"disambiguationData":[OSD([subQ1])],"isStart":false})]})]});var subQ3=makeQuery(id+"F12.imprint","INTERSECT",VERTEX,{"disambiguationData":[OD(0.0)],"derivedFrom":[subQ2,subQ0]});Q20=makeQuery(id+"F12.imprint","IMPRINT",FACE,{"disambiguationData":[TD([[makeQuery(id+"F12.imprint","IMPRINT",EDGE,{"disambiguationData":[TD([[subQ3,1.0]])],"derivedFrom":subQ0}),1.0]])]});}
            extrude(context, id + "F13", {"entities" : qUnion([Q0, Q1, Q2, Q3, Q4, Q5, Q6, Q7, Q8, Q9, Q10, Q11, Q12, Q13, Q14, Q15, Q16, Q17, Q18, Q19, Q20]), "depth" : 10 * mm});
        }
        {
            var Q0;
            Q0=makeQuery(id+"F13.opExtrude","CAP_FACE",FACE,{"disambiguationData":[OSD([sQuery(id+"F0.wireOp",EDGE,"E0.left"),sQuery(id+"F12.wireOp",EDGE,"E13.0"),sQuery(id+"F12.wireOp",EDGE,"E13.1"),sQuery(id+"F12.wireOp",EDGE,"E13.2"),sQuery(id+"F12.wireOp",EDGE,"E13.3"),sQuery(id+"F12.wireOp",EDGE,"E13.4"),sQuery(id+"F12.wireOp",EDGE,"E13.5"),sQuery(id+"F12.wireOp",EDGE,"E15"),sQuery(id+"F12.wireOp",EDGE,"E18"),sQuery(id+"F12.wireOp",EDGE,"E19"),sQuery(id+"F12.wireOp",EDGE,"E20.1.0"),sQuery(id+"F12.wireOp",EDGE,"E20.1.1"),sQuery(id+"F12.wireOp",EDGE,"E20.1.2"),sQuery(id+"F12.wireOp",EDGE,"E20.2.0"),sQuery(id+"F12.wireOp",EDGE,"E20.2.1"),sQuery(id+"F12.wireOp",EDGE,"E20.2.2"),sQuery(id+"F12.wireOp",EDGE,"E20.3.0"),sQuery(id+"F12.wireOp",EDGE,"E20.3.1"),sQuery(id+"F12.wireOp",EDGE,"E20.3.2")])],"isStart":false});
            var sketch = newSketch(context, id + "F14", { "sketchPlane" : qUnion([Q0])});
            skCircle(sketch, "E21", {"center": v(9, -5) * mm, "radius": 2.75 * mm});
            skSolve(sketch);
        }
        {
            var Q0;
            Q0=makeQuery(id+"F14.imprint","IMPRINT",FACE,{"disambiguationData":[TD([[makeQuery(id+"F14.imprint","IMPRINT",EDGE,{"derivedFrom":makeQuery(id+"F13.opExtrude","CAP_EDGE",EDGE,{"disambiguationData":[OSD([sQuery(id+"F12.wireOp",EDGE,"E13.0")])],"isStart":false})}),-1.0]])]});
            var Q1;
            Q1=makeQuery(id+"F14.imprint","IMPRINT",FACE,{"disambiguationData":[TD([[makeQuery(id+"F14.imprint","IMPRINT",EDGE,{"derivedFrom":sQuery(id+"F14.wireOp",EDGE,"E21")}),1.0]])]});
            extrude(context, id + "F15", {"entities" : qUnion([Q0, Q1]), "operationType" : NewBodyOperationType.ADD, "oppositeDirection" : true, "depth" : 3 * mm});
        }
        {
            var Q0;
            Q0=makeQuery(id+"F7.boolean.opBoolean","MERGE",FACE,{"derivedFrom":[makeQuery(id+"F1.opExtrude","SWEPT_FACE",FACE,{"disambiguationData":[OSD([sQuery(id+"F0.wireOp",EDGE,"E0.right")])]}),makeQuery(id+"F7.opExtrude","CAP_FACE",FACE,{"disambiguationData":[OSD([sQuery(id+"F6.wireOp",EDGE,"E6.bottom"),sQuery(id+"F6.wireOp",EDGE,"E6.left"),sQuery(id+"F6.wireOp",EDGE,"E6.right"),sQuery(id+"F6.wireOp",EDGE,"E7"),sQuery(id+"F6.wireOp",EDGE,"E10")])],"isStart":true})]});
            var sketch = newSketch(context, id + "F16", { "sketchPlane" : qUnion([Q0])});
            skCircle(sketch, "E22", {"center": v(-9, -5) * mm, "radius": 5 * mm});
            skCircle(sketch, "E23", {"center": v(-9, -5) * mm, "radius": 2.75 * mm});
            skLineSegment(sketch, "E24", {"start": v(-9, 0) * mm, "end": v(-24, 0) * mm});
            skLineSegment(sketch, "E25", {"start": v(-24, 0) * mm, "end": v(-24, -10) * mm});
            skLineSegment(sketch, "E26", {"start": v(-24, -10) * mm, "end": v(-9, -10) * mm});
            skSolve(sketch);
        }
        {
            var Q0;
            {var subQ1=sQuery(id+"F16.wireOp",EDGE,"E25");Q0=makeQuery(id+"F16.imprint","IMPRINT",FACE,{"disambiguationData":[TD([[makeQuery(id+"F16.imprint","IMPRINT",EDGE,{"derivedFrom":subQ1}),1.0]])]});}
            var Q1;
            Q1=makeQuery(id+"F16.imprint","IMPRINT",FACE,{"disambiguationData":[TD([[makeQuery(id+"F16.imprint","IMPRINT",EDGE,{"derivedFrom":sQuery(id+"F16.wireOp",EDGE,"E23")}),-1.0]])]});
            var Q2;
            {var subQ0=sQuery(id+"F16.wireOp",EDGE,"E24");var subQ1=sQuery(id+"F16.wireOp",EDGE,"E22");var subQ2=makeQuery(id+"F16.imprint","INTERSECT",VERTEX,{"derivedFrom":[subQ1,subQ0]});Q2=makeQuery(id+"F16.imprint","IMPRINT",FACE,{"disambiguationData":[TD([[makeQuery(id+"F16.imprint","IMPRINT",EDGE,{"disambiguationData":[TD([[subQ2,-1.0]])],"derivedFrom":subQ1}),-1.0]])]});}
            var Q3;
            {var subQ0=sQuery(id+"F6.wireOp",EDGE,"E10");var subQ1=sQuery(id+"F6.wireOp",EDGE,"E6.right");var subQ2=sQuery(id+"F6.wireOp",EDGE,"E6.left");var subQ3=sQuery(id+"F0.wireOp",EDGE,"E0.right");var subQ4=makeQuery(id+"F7.boolean.opBoolean","MERGE",FACE,{"derivedFrom":[makeQuery(id+"F1.opExtrude","SWEPT_FACE",FACE,{"disambiguationData":[OSD([subQ3])]}),makeQuery(id+"F7.opExtrude","CAP_FACE",FACE,{"disambiguationData":[OSD([sQuery(id+"F6.wireOp",EDGE,"E6.bottom"),subQ2,subQ1,sQuery(id+"F6.wireOp",EDGE,"E7"),subQ0])],"isStart":true})]});var subQ5=makeQuery(id+"F11.opFillet","BLEND_EDGE",EDGE,{"blendedFrom":[makeQuery(id+"F7.opExtrude","CAP_EDGE",EDGE,{"disambiguationData":[OSD([subQ0])],"isStart":true}),subQ4],"blendedInto":[subQ4]});Q3=makeQuery(id+"F16.imprint","IMPRINT",FACE,{"disambiguationData":[TD([[makeQuery(id+"F16.imprint","IMPRINT",EDGE,{"derivedFrom":subQ5}),-1.0]])]});}
            extrude(context, id + "F17", {"entities" : qUnion([Q0, Q1, Q2, Q3]), "depth" : 5 * mm});
        }
        {
            var Q0;
            Q0=makeQuery(id+"F17.opExtrude","SWEPT_FACE",FACE,{"disambiguationData":[OSD([sQuery(id+"F16.wireOp",EDGE,"E25")])]});
            var sketch = newSketch(context, id + "F18", { "sketchPlane" : qUnion([Q0])});
            skCircle(sketch, "E27", {"center": v(35.5, -5) * mm, "radius": 5 * mm});
            skPoint(sketch, "E28", {"position": v(15.5, -5) * mm});
            skLineSegment(sketch, "E29", {"start": v(20.5, 0) * mm, "end": v(35.5, 0) * mm});
            skLineSegment(sketch, "E30", {"start": v(35.5, -10) * mm, "end": v(20.5, -10) * mm});
            skCircle(sketch, "E31", {"center": v(35.5, -5) * mm, "radius": 2.75 * mm});
            skSolve(sketch);
        }
        {
            var Q0;
            {var subQ0=sQuery(id+"F16.wireOp",EDGE,"E25");Q0=makeQuery(id+"F18.imprint","IMPRINT",FACE,{"disambiguationData":[TD([[makeQuery(id+"F18.imprint","IMPRINT",EDGE,{"derivedFrom":makeQuery(id+"F17.opExtrude","CAP_EDGE",EDGE,{"disambiguationData":[OSD([subQ0])],"isStart":true})}),1.0]])]});}
            var Q1;
            {var subQ0=sQuery(id+"F18.wireOp",EDGE,"E29");Q1=makeQuery(id+"F18.imprint","IMPRINT",FACE,{"disambiguationData":[TD([[makeQuery(id+"F18.imprint","IMPRINT",EDGE,{"derivedFrom":subQ0}),-1.0]])]});}
            var Q2;
            Q2=makeQuery(id+"F18.imprint","IMPRINT",FACE,{"disambiguationData":[TD([[makeQuery(id+"F18.imprint","IMPRINT",EDGE,{"derivedFrom":sQuery(id+"F18.wireOp",EDGE,"E31")}),-1.0]])]});
            var Q3;
            {var subQ0=sQuery(id+"F18.wireOp",EDGE,"E30");Q3=makeQuery(id+"F18.imprint","IMPRINT",FACE,{"disambiguationData":[TD([[makeQuery(id+"F18.imprint","IMPRINT",EDGE,{"derivedFrom":subQ0}),-1.0]])]});}
            extrude(context, id + "F19", {"entities" : qUnion([Q0, Q1, Q2, Q3]), "operationType" : NewBodyOperationType.ADD, "depth" : 5 * mm});
        }
        {
            var Q0;
            Q0=makeQuery(id+"F19.opExtrude","CAP_FACE",FACE,{"disambiguationData":[OSD([sQuery(id+"F16.wireOp",EDGE,"E24"),sQuery(id+"F16.wireOp",EDGE,"E25"),sQuery(id+"F16.wireOp",EDGE,"E26"),sQuery(id+"F18.wireOp",EDGE,"E27"),sQuery(id+"F18.wireOp",EDGE,"E29"),sQuery(id+"F18.wireOp",EDGE,"E30"),sQuery(id+"F18.wireOp",EDGE,"E31")])],"isStart":true});
            var sketch = newSketch(context, id + "F20", { "sketchPlane" : qUnion([Q0])});
            skCircle(sketch, "E32.cCircle", {"center": v(-35.5, -5) * mm, "radius": 4 * mm, "construction": true});
            skLineSegment(sketch, "E32.0", {"start": v(-37.8, -1) * mm, "end": v(-33.2, -1) * mm});
            skLineSegment(sketch, "E32.1", {"start": v(-33.2, -1) * mm, "end": v(-30.88, -5) * mm});
            skLineSegment(sketch, "E32.2", {"start": v(-30.88, -5) * mm, "end": v(-33.2, -9) * mm});
            skLineSegment(sketch, "E32.3", {"start": v(-33.2, -9) * mm, "end": v(-37.8, -9) * mm});
            skLineSegment(sketch, "E32.4", {"start": v(-37.8, -9) * mm, "end": v(-40.12, -5) * mm});
            skLineSegment(sketch, "E32.5", {"start": v(-40.12, -5) * mm, "end": v(-37.8, -1) * mm});
            skPoint(sketch, "E32.0.midPoint", {"position": v(-35.5, -1) * mm});
            skCircle(sketch, "E33", {"center": v(-23.5, -5) * mm, "radius": 1.5 * mm});
            skCircle(sketch, "E34", {"center": v(-35.5, -5) * mm, "radius": 6.62 * mm});
            skLineSegment(sketch, "E35", {"start": v(-35.5, -5) * mm, "end": v(-30.82, -0.32) * mm});
            skLineSegment(sketch, "E36", {"start": v(-35.5, -5) * mm, "end": v(-30.82, -9.68) * mm});
            skArc(sketch, "E37", {"start": v(-23.45, -6.5) * mm, "mid": v(-27.44, -7.39) * mm, "end": v(-30.82, -9.68) * mm});
            skArc(sketch, "E38", {"start": v(-30.82, -0.32) * mm, "mid": v(-27.44, -2.61) * mm, "end": v(-23.45, -3.5) * mm});
            skArc(sketch, "E39.1.0", {"start": v(-34, 7.05) * mm, "mid": v(-33.11, 3.06) * mm, "end": v(-30.82, -0.32) * mm});
            skCircle(sketch, "E39.1.1", {"center": v(-35.5, 7) * mm, "radius": 1.5 * mm});
            skArc(sketch, "E39.1.2", {"start": v(-40.18, -0.32) * mm, "mid": v(-37.89, 3.06) * mm, "end": v(-37, 7.05) * mm});
            skArc(sketch, "E39.2.0", {"start": v(-47.55, -3.5) * mm, "mid": v(-43.56, -2.61) * mm, "end": v(-40.18, -0.32) * mm});
            skCircle(sketch, "E39.2.1", {"center": v(-47.5, -5) * mm, "radius": 1.5 * mm});
            skArc(sketch, "E39.2.2", {"start": v(-40.18, -9.68) * mm, "mid": v(-43.56, -7.39) * mm, "end": v(-47.55, -6.5) * mm});
            skArc(sketch, "E39.3.0", {"start": v(-37, -17.05) * mm, "mid": v(-37.89, -13.06) * mm, "end": v(-40.18, -9.68) * mm});
            skCircle(sketch, "E39.3.1", {"center": v(-35.5, -17) * mm, "radius": 1.5 * mm});
            skArc(sketch, "E39.3.2", {"start": v(-30.82, -9.68) * mm, "mid": v(-33.11, -13.06) * mm, "end": v(-34, -17.05) * mm});
            skSolve(sketch);
        }
        {
            var Q0;
            {var subQ6=makeQuery(id+"F19.opExtrude","CAP_EDGE",EDGE,{"disambiguationData":[OSD([sQuery(id+"F18.wireOp",EDGE,"E27")])],"isStart":true});Q0=makeQuery(id+"F20.imprint","IMPRINT",FACE,{"disambiguationData":[TD([[makeQuery(id+"F20.imprint","IMPRINT",EDGE,{"derivedFrom":subQ6}),1.0]])]});}
            var Q1;
            {var subQ15=sQuery(id+"F20.wireOp",EDGE,"E32.0");Q1=makeQuery(id+"F20.imprint","IMPRINT",FACE,{"disambiguationData":[TD([[makeQuery(id+"F20.imprint","IMPRINT",EDGE,{"derivedFrom":subQ15}),1.0]])]});}
            var Q2;
            {var subQ5=sQuery(id+"F20.wireOp",EDGE,"E32.2");var subQ6=sQuery(id+"F20.wireOp",EDGE,"E32.1");var subQ7=makeQuery(id+"F20.imprint","INTERSECT",VERTEX,{"derivedFrom":[subQ6,subQ5]});Q2=makeQuery(id+"F20.imprint","IMPRINT",FACE,{"disambiguationData":[TD([[makeQuery(id+"F20.imprint","IMPRINT",EDGE,{"disambiguationData":[TD([[subQ7,1.0]])],"derivedFrom":subQ6}),1.0]])]});}
            var Q3;
            {var subQ0=sQuery(id+"F20.wireOp",EDGE,"E37");Q3=makeQuery(id+"F20.imprint","IMPRINT",FACE,{"disambiguationData":[TD([[makeQuery(id+"F20.imprint","IMPRINT",EDGE,{"derivedFrom":subQ0}),-1.0]])]});}
            var Q4;
            {var subQ0=sQuery(id+"F20.wireOp",EDGE,"E33");var subQ1=makeQuery(id+"F20.imprint","INTERSECT",VERTEX,{"derivedFrom":[subQ0,sQuery(id+"F20.wireOp",EDGE,"E37")]});Q4=makeQuery(id+"F20.imprint","IMPRINT",FACE,{"disambiguationData":[TD([[makeQuery(id+"F20.imprint","IMPRINT",EDGE,{"disambiguationData":[TD([[subQ1,1.0]])],"derivedFrom":subQ0}),1.0]])]});}
            var Q5;
            {var subQ18=sQuery(id+"F20.wireOp",EDGE,"E39.1.2");Q5=makeQuery(id+"F20.imprint","IMPRINT",FACE,{"disambiguationData":[TD([[makeQuery(id+"F20.imprint","IMPRINT",EDGE,{"derivedFrom":subQ18}),-1.0]])]});}
            var Q6;
            {var subQ0=sQuery(id+"F20.wireOp",EDGE,"E39.2.1");var subQ1=makeQuery(id+"F20.imprint","INTERSECT",VERTEX,{"derivedFrom":[sQuery(id+"F20.wireOp",EDGE,"E39.2.0"),subQ0]});Q6=makeQuery(id+"F20.imprint","IMPRINT",FACE,{"disambiguationData":[TD([[makeQuery(id+"F20.imprint","IMPRINT",EDGE,{"disambiguationData":[TD([[subQ1,1.0]])],"derivedFrom":subQ0}),1.0]])]});}
            var Q7;
            {var subQ0=sQuery(id+"F20.wireOp",EDGE,"E39.3.1");var subQ1=makeQuery(id+"F20.imprint","INTERSECT",VERTEX,{"derivedFrom":[sQuery(id+"F20.wireOp",EDGE,"E39.3.0"),subQ0]});Q7=makeQuery(id+"F20.imprint","IMPRINT",FACE,{"disambiguationData":[TD([[makeQuery(id+"F20.imprint","IMPRINT",EDGE,{"disambiguationData":[TD([[subQ1,1.0]])],"derivedFrom":subQ0}),1.0]])]});}
            var Q8;
            {var subQ0=sQuery(id+"F20.wireOp",EDGE,"E39.1.1");var subQ1=makeQuery(id+"F20.imprint","INTERSECT",VERTEX,{"derivedFrom":[sQuery(id+"F20.wireOp",EDGE,"E39.1.0"),subQ0]});Q8=makeQuery(id+"F20.imprint","IMPRINT",FACE,{"disambiguationData":[TD([[makeQuery(id+"F20.imprint","IMPRINT",EDGE,{"disambiguationData":[TD([[subQ1,1.0]])],"derivedFrom":subQ0}),1.0]])]});}
            var Q9;
            {var subQ0=sQuery(id+"F20.wireOp",EDGE,"E39.1.0");var subQ1=sQuery(id+"F20.wireOp",EDGE,"E34");var subQ2=makeQuery(id+"F20.imprint","INTERSECT",VERTEX,{"derivedFrom":[subQ1,sQuery(id+"F20.wireOp",EDGE,"E35"),sQuery(id+"F20.wireOp",EDGE,"E38"),subQ0]});Q9=makeQuery(id+"F20.imprint","IMPRINT",FACE,{"disambiguationData":[TD([[makeQuery(id+"F20.imprint","IMPRINT",EDGE,{"disambiguationData":[TD([[subQ2,-1.0]])],"derivedFrom":subQ1}),-1.0]])]});}
            var Q10;
            {var subQ0=sQuery(id+"F20.wireOp",EDGE,"E39.3.2");var subQ1=sQuery(id+"F20.wireOp",EDGE,"E34");var subQ2=makeQuery(id+"F20.imprint","INTERSECT",VERTEX,{"derivedFrom":[subQ1,sQuery(id+"F20.wireOp",EDGE,"E36"),sQuery(id+"F20.wireOp",EDGE,"E37"),subQ0]});Q10=makeQuery(id+"F20.imprint","IMPRINT",FACE,{"disambiguationData":[TD([[makeQuery(id+"F20.imprint","IMPRINT",EDGE,{"disambiguationData":[TD([[subQ2,1.0]])],"derivedFrom":subQ1}),-1.0]])]});}
            extrude(context, id + "F21", {"entities" : qUnion([Q0, Q1, Q2, Q3, Q4, Q5, Q6, Q7, Q8, Q9, Q10]), "depth" : 10 * mm});
        }
        {
            var Q0;
            Q0=makeQuery(id+"F21.opExtrude","CAP_FACE",FACE,{"disambiguationData":[OSD([sQuery(id+"F16.wireOp",EDGE,"E24"),sQuery(id+"F16.wireOp",EDGE,"E25"),sQuery(id+"F16.wireOp",EDGE,"E26"),sQuery(id+"F18.wireOp",EDGE,"E29"),sQuery(id+"F18.wireOp",EDGE,"E30"),sQuery(id+"F20.wireOp",EDGE,"E32.0"),sQuery(id+"F20.wireOp",EDGE,"E32.1"),sQuery(id+"F20.wireOp",EDGE,"E32.2"),sQuery(id+"F20.wireOp",EDGE,"E32.3"),sQuery(id+"F20.wireOp",EDGE,"E32.4"),sQuery(id+"F20.wireOp",EDGE,"E32.5"),sQuery(id+"F20.wireOp",EDGE,"E33"),sQuery(id+"F20.wireOp",EDGE,"E34"),sQuery(id+"F20.wireOp",EDGE,"E37"),sQuery(id+"F20.wireOp",EDGE,"E38"),sQuery(id+"F20.wireOp",EDGE,"E39.1.0"),sQuery(id+"F20.wireOp",EDGE,"E39.1.1"),sQuery(id+"F20.wireOp",EDGE,"E39.1.2"),sQuery(id+"F20.wireOp",EDGE,"E39.2.0"),sQuery(id+"F20.wireOp",EDGE,"E39.2.1"),sQuery(id+"F20.wireOp",EDGE,"E39.2.2"),sQuery(id+"F20.wireOp",EDGE,"E39.3.0"),sQuery(id+"F20.wireOp",EDGE,"E39.3.1"),sQuery(id+"F20.wireOp",EDGE,"E39.3.2")])],"isStart":false});
            var sketch = newSketch(context, id + "F22", { "sketchPlane" : qUnion([Q0])});
            skSolve(sketch);
        }
        {
            var Q0;
            Q0=makeQuery(id+"F22.imprint","IMPRINT",FACE,{"disambiguationData":[TD([[makeQuery(id+"F22.imprint","IMPRINT",EDGE,{"derivedFrom":makeQuery(id+"F21.opExtrude","CAP_EDGE",EDGE,{"disambiguationData":[OSD([sQuery(id+"F20.wireOp",EDGE,"E32.0")])],"isStart":false})}),-1.0]])]});
            extrude(context, id + "F23", {"entities" : qUnion([Q0]), "operationType" : NewBodyOperationType.ADD, "oppositeDirection" : true, "depth" : 4 * mm});
        }
        {
            var Q0;
            Q0=makeQuery(id+"F19.opExtrude","CAP_FACE",FACE,{"disambiguationData":[OSD([sQuery(id+"F16.wireOp",EDGE,"E24"),sQuery(id+"F16.wireOp",EDGE,"E25"),sQuery(id+"F16.wireOp",EDGE,"E26"),sQuery(id+"F18.wireOp",EDGE,"E27"),sQuery(id+"F18.wireOp",EDGE,"E29"),sQuery(id+"F18.wireOp",EDGE,"E30"),sQuery(id+"F18.wireOp",EDGE,"E31")])],"isStart":false});
            var sketch = newSketch(context, id + "F24", { "sketchPlane" : qUnion([Q0])});
            skCircle(sketch, "E40", {"center": v(35.5, -5) * mm, "radius": 5 * mm});
            skCircle(sketch, "E41", {"center": v(35.5, -5) * mm, "radius": 2.75 * mm});
            skLineSegment(sketch, "E42", {"start": v(30.5, -5) * mm, "end": v(30.5, -23.5) * mm});
            skLineSegment(sketch, "E43", {"start": v(40.5, -5) * mm, "end": v(40.5, -23.5) * mm});
            skLineSegment(sketch, "E44.bottom", {"start": v(40.5, -23.5) * mm, "end": v(10.5, -23.5) * mm});
            skLineSegment(sketch, "E44.top", {"start": v(40.5, -28.5) * mm, "end": v(10.5, -28.5) * mm});
            skLineSegment(sketch, "E44.left", {"start": v(40.5, -23.5) * mm, "end": v(40.5, -28.5) * mm});
            skLineSegment(sketch, "E44.right", {"start": v(10.5, -23.5) * mm, "end": v(10.5, -28.5) * mm});
            skPoint(sketch, "E45", {"position": v(35.5, -34.01) * mm});
            skPoint(sketch, "E46", {"position": v(15.5, -23.5) * mm});
            skSolve(sketch);
        }
        {
            var Q0;
            {var subQ3=sQuery(id+"F24.wireOp",EDGE,"E43");Q0=makeQuery(id+"F24.imprint","IMPRINT",FACE,{"disambiguationData":[TD([[makeQuery(id+"F24.imprint","IMPRINT",EDGE,{"derivedFrom":subQ3}),-1.0]])]});}
            var Q1;
            Q1=makeQuery(id+"F24.imprint","IMPRINT",FACE,{"disambiguationData":[TD([[makeQuery(id+"F24.imprint","IMPRINT",EDGE,{"derivedFrom":sQuery(id+"F24.wireOp",EDGE,"E44.top")}),-1.0]])]});
            var Q2;
            Q2=makeQuery(id+"F24.imprint","IMPRINT",FACE,{"disambiguationData":[TD([[makeQuery(id+"F24.imprint","IMPRINT",EDGE,{"derivedFrom":sQuery(id+"F24.wireOp",EDGE,"E41")}),-1.0]])]});
            var Q3;
            {var subQ0=sQuery(id+"F24.wireOp",EDGE,"E40");var subQ3=sQuery(id+"F24.wireOp",EDGE,"E42");var subQ4=makeQuery(id+"F24.imprint","INTERSECT",VERTEX,{"derivedFrom":[subQ0,subQ3]});Q3=makeQuery(id+"F24.imprint","IMPRINT",FACE,{"disambiguationData":[TD([[makeQuery(id+"F24.imprint","IMPRINT",EDGE,{"disambiguationData":[TD([[subQ4,-1.0]])],"derivedFrom":subQ0}),-1.0]])]});}
            extrude(context, id + "F25", {"entities" : qUnion([Q0, Q1, Q2, Q3]), "depth" : 6 * mm});
        }
        {
            var Q0;
            Q0=makeQuery(id+"F25.opExtrude","CAP_FACE",FACE,{"disambiguationData":[OSD([sQuery(id+"F24.wireOp",EDGE,"E40"),sQuery(id+"F24.wireOp",EDGE,"E41"),sQuery(id+"F24.wireOp",EDGE,"E42"),sQuery(id+"F24.wireOp",EDGE,"E43"),sQuery(id+"F24.wireOp",EDGE,"E44.bottom"),sQuery(id+"F24.wireOp",EDGE,"E44.top"),sQuery(id+"F24.wireOp",EDGE,"E44.left"),sQuery(id+"F24.wireOp",EDGE,"E44.right")])],"isStart":true});
            var sketch = newSketch(context, id + "F26", { "sketchPlane" : qUnion([Q0])});
            skLineSegment(sketch, "E47.bottom", {"start": v(-10.5, -23.5) * mm, "end": v(-40.5, -23.5) * mm});
            skLineSegment(sketch, "E47.top", {"start": v(-10.5, -28.5) * mm, "end": v(-40.5, -28.5) * mm});
            skLineSegment(sketch, "E47.left", {"start": v(-10.5, -23.5) * mm, "end": v(-10.5, -28.5) * mm});
            skLineSegment(sketch, "E47.right", {"start": v(-40.5, -23.5) * mm, "end": v(-40.5, -28.5) * mm});
            skSolve(sketch);
        }
        {
            var Q0;
            Q0 = qSketchRegion(id + "F26", true);
            extrude(context, id + "F27", {"entities" : qUnion([Q0]), "operationType" : NewBodyOperationType.ADD, "depth" : 25 * mm});
        }
        {
            var Q0;
            Q0=makeQuery(id+"F27.boolean.opBoolean","MERGE",FACE,{"derivedFrom":[makeQuery(id+"F25.opExtrude","SWEPT_FACE",FACE,{"disambiguationData":[OSD([sQuery(id+"F24.wireOp",EDGE,"E44.bottom")])]}),makeQuery(id+"F27.opExtrude","SWEPT_FACE",FACE,{"disambiguationData":[OSD([sQuery(id+"F26.wireOp",EDGE,"E47.bottom")])]})]});
            var sketch = newSketch(context, id + "F28", { "sketchPlane" : qUnion([Q0])});
            skPoint(sketch, "E48", {"position": v(15.5, -30) * mm});
            skPoint(sketch, "E49", {"position": v(35.5, -9) * mm});
            skSolve(sketch);
        }
        {
            var Q0;
            Q0=sQuery(id+"F28.wireOp",VERTEX,"E48");
            var Q1;
            Q1=sQuery(id+"F28.wireOp",VERTEX,"E49");
            var Q2;
            Q2=makeQuery(id+"F25.opExtrude","SWEPT_BODY",BODY,{"disambiguationData":[OSD([sQuery(id+"F24.wireOp",EDGE,"E40"),sQuery(id+"F24.wireOp",EDGE,"E41"),sQuery(id+"F24.wireOp",EDGE,"E42"),sQuery(id+"F24.wireOp",EDGE,"E43"),sQuery(id+"F24.wireOp",EDGE,"E44.bottom"),sQuery(id+"F24.wireOp",EDGE,"E44.top"),sQuery(id+"F24.wireOp",EDGE,"E44.left"),sQuery(id+"F24.wireOp",EDGE,"E44.right")])]});
            hole(context, id + "F29", {"style" : HoleStyle.SIMPLE, "endStyle" : HoleEndStyle.THROUGH, "standardTappedOrClearance" : lookupTablePath({ "standard" : "ISO", "fit" : "Normal", "size" : "M5", "type" : "Clearance" }), "standardBlindInLast" : lookupTablePath({ "fit" : "Standard", "standard" : "ISO", "size" : "M5", "type" : "Clearance" }), "holeDiameter" : 5.5 * mm, "tappedDepth" : 13.2 * mm, "tapClearance" : 3, "startFromSketch" : true, "locations" : qUnion([Q0, Q1]), "scope" : qUnion([Q2])});
        }
        {
            var Q0;
            Q0=makeQuery(id+"F27.boolean.opBoolean","MERGE",FACE,{"derivedFrom":[makeQuery(id+"F25.opExtrude","SWEPT_FACE",FACE,{"disambiguationData":[OSD([sQuery(id+"F24.wireOp",EDGE,"E44.top")])]}),makeQuery(id+"F27.opExtrude","SWEPT_FACE",FACE,{"disambiguationData":[OSD([sQuery(id+"F26.wireOp",EDGE,"E47.top")])]})]});
            var sketch = newSketch(context, id + "F30", { "sketchPlane" : qUnion([Q0])});
            skCircle(sketch, "E50", {"center": v(15.5, 30) * mm, "radius": 5 * mm});
            skCircle(sketch, "E51", {"center": v(35.5, 9) * mm, "radius": 5 * mm});
            skLineSegment(sketch, "E52", {"start": v(15.52, 25) * mm, "end": v(30.45, 25.05) * mm});
            skLineSegment(sketch, "E53", {"start": v(30.45, 25.05) * mm, "end": v(30.5, 8.98) * mm});
            skSolve(sketch);
        }
        {
            var Q0;
            {var subQ0=sQuery(id+"F30.wireOp",EDGE,"E50");var subQ1=sQuery(id+"F24.wireOp",EDGE,"E44.top");var subQ4=makeQuery(id+"F25.opExtrude","CAP_EDGE",EDGE,{"disambiguationData":[OSD([subQ1])],"isStart":false});var subQ5=makeQuery(id+"F30.imprint","INTERSECT",VERTEX,{"derivedFrom":[subQ4,subQ0]});Q0=makeQuery(id+"F30.imprint","IMPRINT",FACE,{"disambiguationData":[TD([[makeQuery(id+"F30.imprint","IMPRINT",EDGE,{"disambiguationData":[TD([[subQ5,-1.0]])],"derivedFrom":subQ0}),-1.0]])]});}
            var Q1;
            {var subQ7=sQuery(id+"F30.wireOp",EDGE,"E52");Q1=makeQuery(id+"F30.imprint","IMPRINT",FACE,{"disambiguationData":[TD([[makeQuery(id+"F30.imprint","IMPRINT",EDGE,{"derivedFrom":subQ7}),-1.0]])]});}
            var Q2;
            {var subQ0=sQuery(id+"F30.wireOp",EDGE,"E51");var subQ1=sQuery(id+"F26.wireOp",EDGE,"E47.top");var subQ4=makeQuery(id+"F27.opExtrude","CAP_EDGE",EDGE,{"disambiguationData":[OSD([subQ1])],"isStart":false});var subQ5=makeQuery(id+"F30.imprint","INTERSECT",VERTEX,{"derivedFrom":[subQ4,subQ0]});Q2=makeQuery(id+"F30.imprint","IMPRINT",FACE,{"disambiguationData":[TD([[makeQuery(id+"F30.imprint","IMPRINT",EDGE,{"disambiguationData":[TD([[subQ5,-1.0]])],"derivedFrom":subQ0}),-1.0]])]});}
            extrude(context, id + "F31", {"entities" : qUnion([Q0, Q1, Q2]), "operationType" : NewBodyOperationType.REMOVE, "endBound" : BoundingType.UP_TO_NEXT, "oppositeDirection" : true, "depth" : 25 * mm});
        }
        {
            var Q0;
            Q0=makeQuery(id+"F13.opExtrude","CAP_EDGE",EDGE,{"disambiguationData":[OSD([sQuery(id+"F12.wireOp",EDGE,"E18")])],"isStart":false});
            var Q1;
            Q1=makeQuery(id+"F13.opExtrude","CAP_EDGE",EDGE,{"disambiguationData":[OSD([sQuery(id+"F12.wireOp",EDGE,"E20.1.1")])],"isStart":false});
            var Q2;
            Q2=makeQuery(id+"F13.opExtrude","CAP_EDGE",EDGE,{"disambiguationData":[OSD([sQuery(id+"F12.wireOp",EDGE,"E20.2.1")])],"isStart":false});
            var Q3;
            Q3=makeQuery(id+"F13.opExtrude","CAP_EDGE",EDGE,{"disambiguationData":[OSD([sQuery(id+"F12.wireOp",EDGE,"E20.3.2")])],"isStart":false});
            var Q4;
            Q4=makeQuery(id+"F13.opExtrude","CAP_EDGE",EDGE,{"disambiguationData":[OSD([sQuery(id+"F12.wireOp",EDGE,"E20.2.2")])],"isStart":false});
            var Q5;
            Q5=makeQuery(id+"F13.opExtrude","CAP_EDGE",EDGE,{"disambiguationData":[OSD([sQuery(id+"F12.wireOp",EDGE,"E20.1.2")])],"isStart":false});
            var Q6;
            Q6=makeQuery(id+"F13.opExtrude","CAP_EDGE",EDGE,{"disambiguationData":[OSD([sQuery(id+"F12.wireOp",EDGE,"E20.1.2")])],"isStart":true});
            var Q7;
            Q7=makeQuery(id+"F13.opExtrude","CAP_EDGE",EDGE,{"disambiguationData":[OSD([sQuery(id+"F12.wireOp",EDGE,"E20.3.2")])],"isStart":true});
            var Q8;
            Q8=makeQuery(id+"F13.opExtrude","CAP_EDGE",EDGE,{"disambiguationData":[OSD([sQuery(id+"F12.wireOp",EDGE,"E20.2.2")])],"isStart":true});
            fillet(context, id + "F32", {"entities" : qUnion([Q0, Q1, Q2, Q3, Q4, Q5, Q6, Q7, Q8]), "radius" : 1 * mm, "tangentPropagation" : true, "allowEdgeOverflow" : false});
        }
        {
            var Q0;
            Q0=makeQuery(id+"F19.opExtrude","CAP_EDGE",EDGE,{"disambiguationData":[OSD([sQuery(id+"F16.wireOp",EDGE,"E24"),sQuery(id+"F16.wireOp",EDGE,"E25"),sQuery(id+"F18.wireOp",EDGE,"E29")])],"isStart":true});
            var Q1;
            Q1=makeQuery(id+"F17.opExtrude","CAP_EDGE",EDGE,{"disambiguationData":[OSD([sQuery(id+"F16.wireOp",EDGE,"E24")])],"isStart":false});
            var Q2;
            {var subQ0=sQuery(id+"F16.wireOp",EDGE,"E24");Q2=makeQuery(id+"F19.boolean.opBoolean","MERGE",EDGE,{"derivedFrom":[makeQuery(id+"F17.opExtrude","CAP_EDGE",EDGE,{"disambiguationData":[OSD([subQ0])],"isStart":true}),makeQuery(id+"F19.opExtrude","SWEPT_EDGE",EDGE,{"disambiguationData":[OSD([subQ0,sQuery(id+"F16.wireOp",EDGE,"E25")])]})]});}
            var Q3;
            Q3=makeQuery(id+"F19.opExtrude","CAP_EDGE",EDGE,{"disambiguationData":[OSD([sQuery(id+"F16.wireOp",EDGE,"E25")])],"isStart":false});
            var Q4;
            Q4=makeQuery(id+"F19.opExtrude","CAP_EDGE",EDGE,{"disambiguationData":[OSD([sQuery(id+"F16.wireOp",EDGE,"E24"),sQuery(id+"F16.wireOp",EDGE,"E25"),sQuery(id+"F18.wireOp",EDGE,"E29")])],"isStart":false});
            fillet(context, id + "F33", {"entities" : qUnion([Q0, Q1, Q2, Q3, Q4]), "radius" : 1 * mm, "tangentPropagation" : true, "allowEdgeOverflow" : false});
        }
        {
            var Q0;
            Q0=makeQuery(id+"F21.opExtrude","CAP_EDGE",EDGE,{"disambiguationData":[OSD([sQuery(id+"F20.wireOp",EDGE,"E33")])],"isStart":false});
            var Q1;
            Q1=makeQuery(id+"F21.opExtrude","CAP_EDGE",EDGE,{"disambiguationData":[OSD([sQuery(id+"F20.wireOp",EDGE,"E39.2.1")])],"isStart":true});
            fillet(context, id + "F34", {"entities" : qUnion([Q0, Q1]), "radius" : 1 * mm, "tangentPropagation" : true, "allowEdgeOverflow" : false});
        }
        {
            var Q0;
            Q0=makeQuery(id+"F25.opExtrude","CAP_EDGE",EDGE,{"disambiguationData":[OSD([sQuery(id+"F24.wireOp",EDGE,"E40")])],"isStart":false});
            var Q1;
            {var subQ0=sQuery(id+"F30.wireOp",EDGE,"E50");var subQ1=sQuery(id+"F24.wireOp",EDGE,"E44.top");var subQ3=makeQuery(id+"F27.boolean.opBoolean","MERGE",FACE,{"derivedFrom":[makeQuery(id+"F25.opExtrude","SWEPT_FACE",FACE,{"disambiguationData":[OSD([sQuery(id+"F24.wireOp",EDGE,"E44.bottom")])]}),makeQuery(id+"F27.opExtrude","SWEPT_FACE",FACE,{"disambiguationData":[OSD([sQuery(id+"F26.wireOp",EDGE,"E47.bottom")])]})]});Q1=makeQuery(id+"F31.boolean.opBoolean","TWEAK_EDGE",EDGE,{"derivedFrom":[makeQuery(id+"F31.opExtrude","TWEAK_EDGE",EDGE,{"derivedFrom":[subQ3,makeQuery(id+"F30.imprint","IMPRINT",EDGE,{"disambiguationData":[TD([[makeQuery(id+"F30.imprint","INTERSECT",VERTEX,{"derivedFrom":[makeQuery(id+"F25.opExtrude","CAP_EDGE",EDGE,{"disambiguationData":[OSD([subQ1])],"isStart":false}),subQ0]}),-1.0]])],"derivedFrom":subQ0})]}),makeQuery(id+"F31.opExtrude","TWEAK_EDGE",EDGE,{"derivedFrom":[subQ3,makeQuery(id+"F30.imprint","IMPRINT",EDGE,{"disambiguationData":[TD([[makeQuery(id+"F30.imprint","INTERSECT",VERTEX,{"derivedFrom":[subQ0,sQuery(id+"F30.wireOp",EDGE,"E52")]}),1.0]])],"derivedFrom":subQ0})]})]});}
            var Q2;
            Q2=makeQuery(id+"F25.opExtrude","CAP_EDGE",EDGE,{"disambiguationData":[OSD([sQuery(id+"F24.wireOp",EDGE,"E40")])],"isStart":true});
            var Q3;
            {var subQ0=sQuery(id+"F30.wireOp",EDGE,"E50");var subQ1=sQuery(id+"F24.wireOp",EDGE,"E44.top");Q3=makeQuery(id+"F31.boolean.opBoolean","TWEAK_EDGE",EDGE,{"derivedFrom":[makeQuery(id+"F31.opExtrude","CAP_EDGE",EDGE,{"disambiguationData":[OSD([subQ0]),TDD([makeQuery(id+"F30.imprint","IMPRINT",EDGE,{"disambiguationData":[TD([[makeQuery(id+"F30.imprint","INTERSECT",VERTEX,{"derivedFrom":[makeQuery(id+"F25.opExtrude","CAP_EDGE",EDGE,{"disambiguationData":[OSD([subQ1])],"isStart":false}),subQ0]}),-1.0]])],"derivedFrom":subQ0})])],"isStart":true}),makeQuery(id+"F31.opExtrude","CAP_EDGE",EDGE,{"disambiguationData":[OSD([subQ0]),TDD([makeQuery(id+"F30.imprint","IMPRINT",EDGE,{"disambiguationData":[TD([[makeQuery(id+"F30.imprint","INTERSECT",VERTEX,{"derivedFrom":[subQ0,sQuery(id+"F30.wireOp",EDGE,"E52")]}),1.0]])],"derivedFrom":subQ0})])],"isStart":true})]});}
            var Q4;
            {var subQ0=sQuery(id+"F30.wireOp",EDGE,"E51");var subQ1=sQuery(id+"F26.wireOp",EDGE,"E47.top");var subQ2=makeQuery(id+"F30.imprint","INTERSECT",VERTEX,{"derivedFrom":[makeQuery(id+"F27.opExtrude","CAP_EDGE",EDGE,{"disambiguationData":[OSD([subQ1])],"isStart":false}),subQ0]});Q4=makeQuery(id+"F31.boolean.opBoolean","TWEAK_EDGE",EDGE,{"derivedFrom":[makeQuery(id+"F31.opExtrude","CAP_EDGE",EDGE,{"disambiguationData":[OSD([subQ0]),TDD([makeQuery(id+"F30.imprint","IMPRINT",EDGE,{"disambiguationData":[TD([[makeQuery(id+"F30.imprint","INTERSECT",VERTEX,{"derivedFrom":[subQ0,sQuery(id+"F30.wireOp",EDGE,"E53")]}),-1.0]])],"derivedFrom":subQ0})])],"isStart":true}),makeQuery(id+"F31.opExtrude","CAP_EDGE",EDGE,{"disambiguationData":[OSD([subQ0]),TDD([makeQuery(id+"F30.imprint","IMPRINT",EDGE,{"disambiguationData":[TD([[subQ2,-1.0]])],"derivedFrom":subQ0})])],"isStart":true})]});}
            var Q5;
            {var subQ0=sQuery(id+"F30.wireOp",EDGE,"E51");var subQ1=sQuery(id+"F26.wireOp",EDGE,"E47.top");var subQ2=makeQuery(id+"F30.imprint","INTERSECT",VERTEX,{"derivedFrom":[makeQuery(id+"F27.opExtrude","CAP_EDGE",EDGE,{"disambiguationData":[OSD([subQ1])],"isStart":false}),subQ0]});var subQ3=makeQuery(id+"F27.boolean.opBoolean","MERGE",FACE,{"derivedFrom":[makeQuery(id+"F25.opExtrude","SWEPT_FACE",FACE,{"disambiguationData":[OSD([sQuery(id+"F24.wireOp",EDGE,"E44.bottom")])]}),makeQuery(id+"F27.opExtrude","SWEPT_FACE",FACE,{"disambiguationData":[OSD([sQuery(id+"F26.wireOp",EDGE,"E47.bottom")])]})]});Q5=makeQuery(id+"F31.boolean.opBoolean","TWEAK_EDGE",EDGE,{"derivedFrom":[makeQuery(id+"F31.opExtrude","TWEAK_EDGE",EDGE,{"derivedFrom":[subQ3,makeQuery(id+"F30.imprint","IMPRINT",EDGE,{"disambiguationData":[TD([[makeQuery(id+"F30.imprint","INTERSECT",VERTEX,{"derivedFrom":[subQ0,sQuery(id+"F30.wireOp",EDGE,"E53")]}),-1.0]])],"derivedFrom":subQ0})]}),makeQuery(id+"F31.opExtrude","TWEAK_EDGE",EDGE,{"derivedFrom":[subQ3,makeQuery(id+"F30.imprint","IMPRINT",EDGE,{"disambiguationData":[TD([[subQ2,-1.0]])],"derivedFrom":subQ0})]})]});}
            var Q6;
            Q6=makeQuery(id+"F27.opExtrude","CAP_EDGE",EDGE,{"disambiguationData":[OSD([sQuery(id+"F26.wireOp",EDGE,"E47.bottom")])],"isStart":true});
            fillet(context, id + "F35", {"entities" : qUnion([Q0, Q1, Q2, Q3, Q4, Q5, Q6]), "radius" : 1 * mm, "tangentPropagation" : true, "allowEdgeOverflow" : false});
        }
    });
